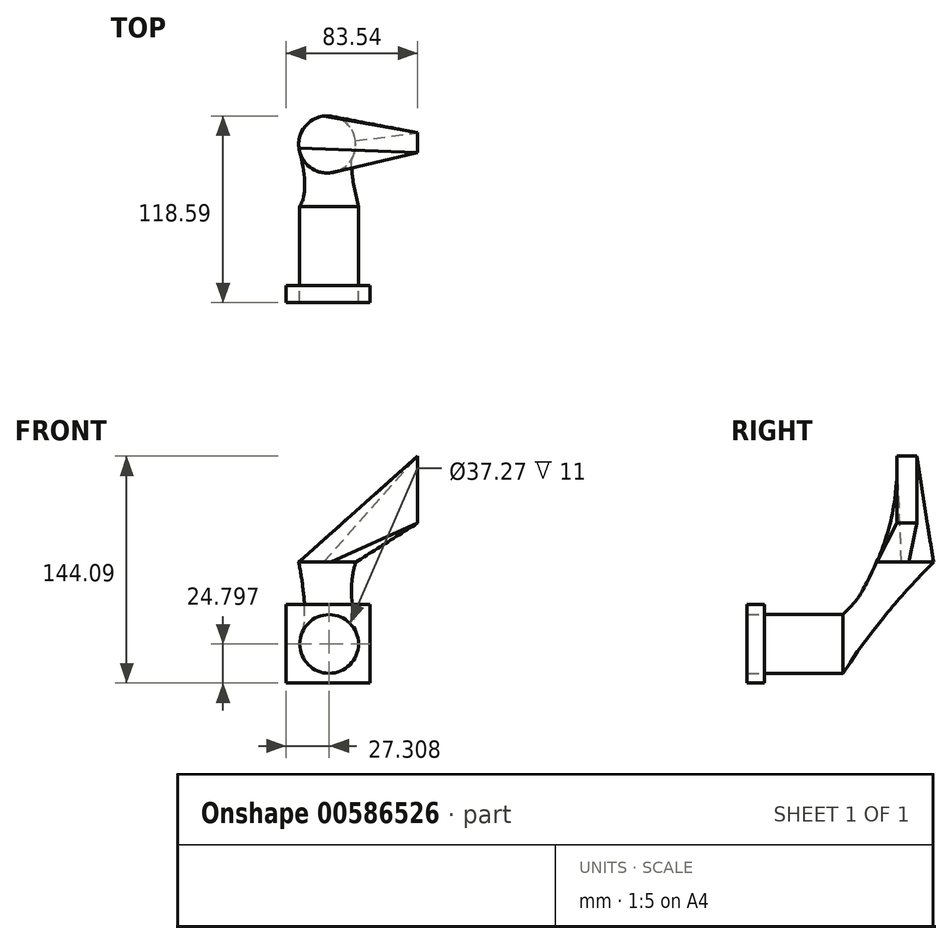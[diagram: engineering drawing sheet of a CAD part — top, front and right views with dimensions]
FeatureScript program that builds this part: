
annotation { "Feature Type Name" : "Feature", "Feature Type Description" : "" }
export const myFeature = defineFeature(function(context is Context, id is Id, definition is map)
    precondition{}
    {
        {
            var Q0;
            Q0=qCreatedBy(makeId("Front.planeOp"),FACE);
            var sketch = newSketch(context, id + "F0", { "sketchPlane" : qUnion([Q0])});
            skCircle(sketch, "E0", {"center": v(-56.23, -51.97) * mm, "radius": 18.63 * mm});
            skSolve(sketch);
        }
        {
            var Q0;
            Q0=qCreatedBy(makeId("Top.planeOp"),FACE);
            var sketch = newSketch(context, id + "F1", { "sketchPlane" : qUnion([Q0])});
            skCircle(sketch, "E1", {"center": v(-57.4, 39.46) * mm, "radius": 18.13 * mm});
            skSolve(sketch);
        }
        {
            var Q0;
            Q0=makeQuery(id+"F1.imprint","IMPRINT",FACE,{"disambiguationData":[TD([[makeQuery(id+"F1.imprint","IMPRINT",EDGE,{"derivedFrom":sQuery(id+"F1.wireOp",EDGE,"E1")}),1.0]])]});
            var Q1;
            Q1=makeQuery(id+"F0.imprint","IMPRINT",FACE,{"disambiguationData":[TD([[makeQuery(id+"F0.imprint","IMPRINT",EDGE,{"derivedFrom":sQuery(id+"F0.wireOp",EDGE,"E0")}),1.0]])]});
            loft(context, id + "F2", {"sheetProfilesArray" : [{ "sheetProfileEntities" : qUnion([Q0]) }, { "sheetProfileEntities" : qUnion([Q1]) }]});
        }
        {
            var Q0;
            Q0=qCreatedBy(makeId("Right.planeOp"),FACE);
            var sketch = newSketch(context, id + "F3", { "sketchPlane" : qUnion([Q0])});
            skLineSegment(sketch, "E2.bottom", {"start": v(46.9, 24.8) * mm, "end": v(34.39, 24.8) * mm});
            skLineSegment(sketch, "E2.top", {"start": v(46.9, 67.32) * mm, "end": v(34.39, 67.32) * mm});
            skLineSegment(sketch, "E2.left", {"start": v(46.9, 24.8) * mm, "end": v(46.9, 67.32) * mm});
            skLineSegment(sketch, "E2.right", {"start": v(34.39, 24.8) * mm, "end": v(34.39, 67.32) * mm});
            skPoint(sketch, "E2.middle", {"position": v(40.64, 46.06) * mm});
            skSolve(sketch);
        }
        {
            var Q1;
            Q1=makeQuery(id+"F2.opLoft","CAP_FACE",FACE,{"disambiguationData":[OSD([makeQuery(id+"F1.imprint","IMPRINT",FACE,{"disambiguationData":[TD([[makeQuery(id+"F1.imprint","IMPRINT",EDGE,{"derivedFrom":sQuery(id+"F1.wireOp",EDGE,"E1")}),1.0]])]})])],"isStart":true});
            var Q2;
            Q2=makeQuery(id+"F3.imprint","IMPRINT",FACE,{"disambiguationData":[TD([[makeQuery(id+"F3.imprint","IMPRINT",EDGE,{"derivedFrom":sQuery(id+"F3.wireOp",EDGE,"E2.bottom")}),-1.0]])]});
            loft(context, id + "F4", {"sheetProfilesArray" : [{ "sheetProfileEntities" : qUnion([Q1]) }, { "sheetProfileEntities" : qUnion([Q2]) }]});
        }
        {
            var Q0;
            Q0=makeQuery(id+"F2.opLoft","CAP_FACE",FACE,{"disambiguationData":[OSD([makeQuery(id+"F0.imprint","IMPRINT",FACE,{"disambiguationData":[TD([[makeQuery(id+"F0.imprint","IMPRINT",EDGE,{"derivedFrom":sQuery(id+"F0.wireOp",EDGE,"E0")}),1.0]])]})])],"isStart":true});
            extrude(context, id + "F5", {"entities" : qUnion([Q0]), "operationType" : NewBodyOperationType.ADD, "depth" : 50 * mm, "offsetDistance" : 25 * mm});
        }
        {
            var Q0;
            Q0=makeQuery(id+"F5.opExtrude","CAP_FACE",FACE,{"disambiguationData":[OSD([makeQuery(id+"F0.imprint","IMPRINT",FACE,{"disambiguationData":[TD([[makeQuery(id+"F0.imprint","IMPRINT",EDGE,{"derivedFrom":sQuery(id+"F0.wireOp",EDGE,"E0")}),1.0]])]})])],"isStart":false});
            var sketch = newSketch(context, id + "F6", { "sketchPlane" : qUnion([Q0])});
            skLineSegment(sketch, "E3.bottom", {"start": v(-83.54, -76.77) * mm, "end": v(-30.18, -76.77) * mm});
            skLineSegment(sketch, "E3.top", {"start": v(-83.54, -26.75) * mm, "end": v(-30.18, -26.75) * mm});
            skLineSegment(sketch, "E3.left", {"start": v(-83.54, -76.77) * mm, "end": v(-83.54, -26.75) * mm});
            skLineSegment(sketch, "E3.right", {"start": v(-30.18, -76.77) * mm, "end": v(-30.18, -26.75) * mm});
            skPoint(sketch, "E3.middle", {"position": v(-56.86, -51.76) * mm});
            skSolve(sketch);
        }
        {
            var Q0;
            Q0=makeQuery(id+"F6.imprint","IMPRINT",FACE,{"disambiguationData":[TD([[makeQuery(id+"F6.imprint","IMPRINT",EDGE,{"derivedFrom":sQuery(id+"F6.wireOp",EDGE,"E3.bottom")}),1.0]])]});
            extrude(context, id + "F7", {"entities" : qUnion([Q0]), "depth" : 11 * mm, "offsetDistance" : 25 * mm});
        }
    });
